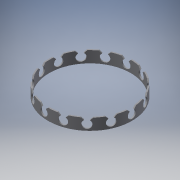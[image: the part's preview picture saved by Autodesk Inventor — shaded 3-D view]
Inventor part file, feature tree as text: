
AUTODESK INVENTOR PART (.ipt)
format: ipt  version: 2018 (Build 220112000, 112)  size: 266,240 bytes
history: native  units: in
note: dims shown in document units (in); Inventor stores cm internally (conversion verified against a paired STEP export)
features: extrude x3, sketch x3, mirror x1, pattern_circular x1
ambient origin geometry x8: Origin, YZ Plane, XZ Plane, XY Plane, X Axis, Y Axis, Z Axis, Center Point
bodies: Solid1 (feature_tree)
feature tree (8):
  extrude  "Extrusion1"  Depth=3.57in
  extrude  "Extrusion2"  Depth=0.3in
  sketch  "Sketch3"  dims[d5=0.25in d6=3.0625in d7=0.0in d8=0.35in d9=0.25in d11=45.0deg d14=0.0938in d17=5.9055in d18=360.0deg d21=0.08in d25=3.0625in d26=0.0in]
  extrude  "Extrusion5"  Depth=0.25in TaperAngle=0.0deg
  mirror  "Mirror3"
  pattern_circular  "Circular Pattern1"  [2 undecoded]
  sketch  "Sketch1"  dims[d0=3.68in d1=3.57in]
  sketch  "Sketch2"  dims[d2=0.5in d3=0.0in d4=0.3in]
note: 2 required parameter values undecoded (feature->parameter linkage not recoverable at this tier; creation-order binding heuristic only, values carry confidence <= 0.55)
